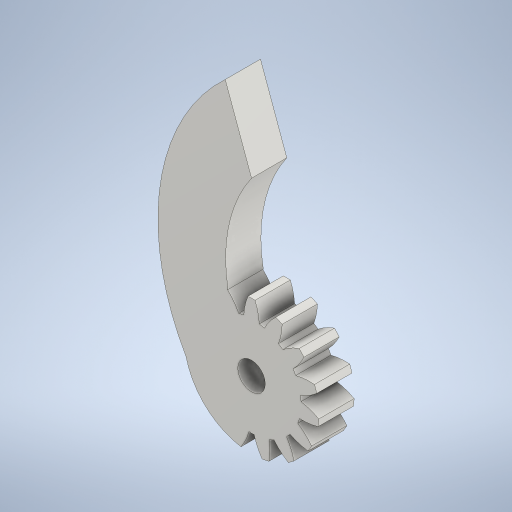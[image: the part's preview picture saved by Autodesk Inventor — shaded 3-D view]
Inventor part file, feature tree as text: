
AUTODESK INVENTOR PART (.ipt)
format: ipt  version: 2024 (Build 280153000, 153)  size: 638,976 bytes
history: native  units: mm (DEFAULTED — no unit token found)
features: extrude x3, plane x3, other x3, sketch x3, projected_geometry x1
ambient origin geometry x8: Origin, YZ Plane, XZ Plane, XY Plane, X Axis, Y Axis, Z Axis, Center Point
bodies: Solid1 (feature_tree)
feature tree (13):
  extrude  "Extrusion1"  Depth=6.666667mm TaperAngle=0.0deg
  plane  "Work Plane2"
  plane  "Work Plane8"
  plane  "Work Plane9"
  other  "Spur Gear"
  extrude  "Extrusion2"  Depth=10.0mm TaperAngle=0.0deg
  extrude  "Extrusion4"  Depth=10.0mm TaperAngle=0.0deg
  sketch  "Sketch1"  dims[d0=25.492855mm d1=6.666667mm d2=0.0mm]
  other  "Srf1"
  sketch  "Sketch3"  dims[d3=22.5mm d4=10.0mm d5=0.0mm]
  sketch  "Sketch7"  dims[d16=23.4mm d17=0.0mm d34=2.094395mm d39=0.0mm d41=0.0mm d43=23.4mm d46=23.4mm d47=0.0mm d48=0.0mm d49=5.2mm d50=10.0mm d51=0.0mm d64=50.0mm d68=54.037661mm d69=22.118mm d70=16.88mm d71=79.653868mm d72=3.490659mm d73=10.0mm d74=0.0mm]
  projected_geometry  "Projected Loop2"
  other  "Pitch Diameter"
